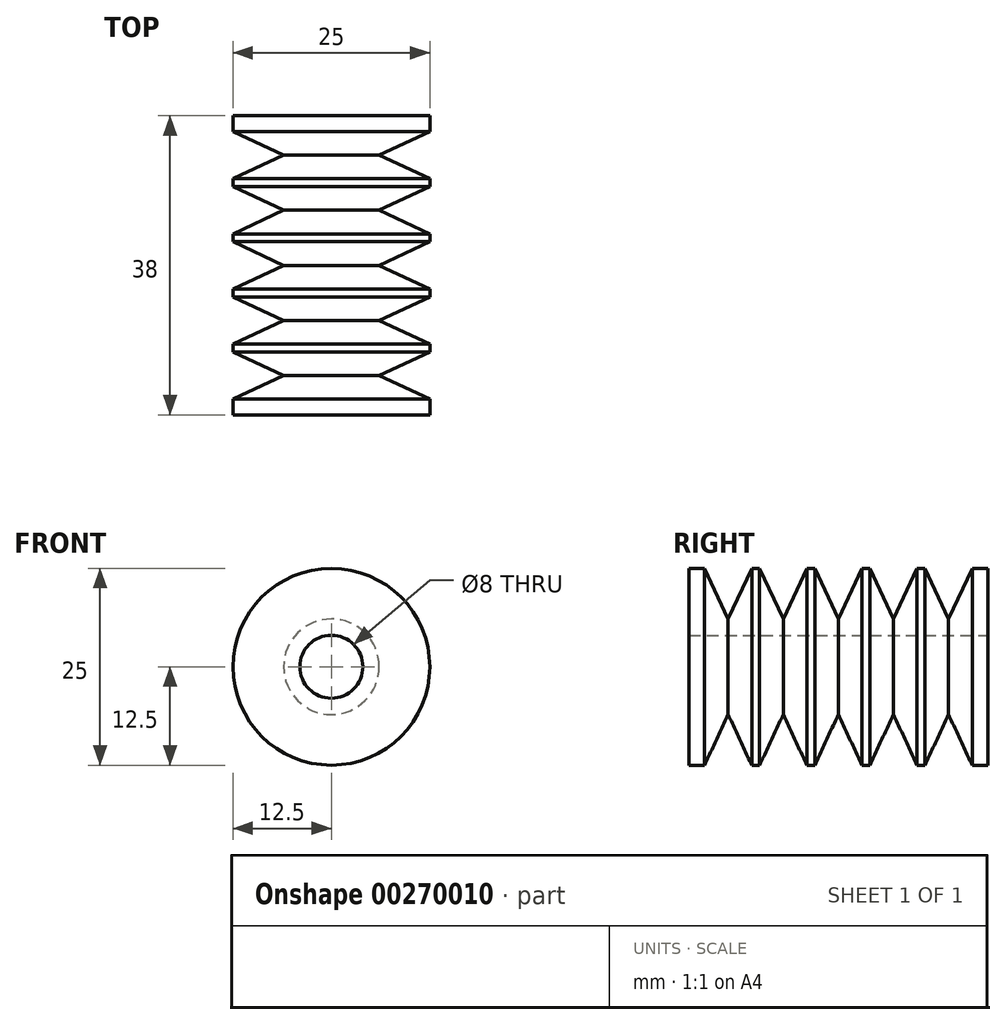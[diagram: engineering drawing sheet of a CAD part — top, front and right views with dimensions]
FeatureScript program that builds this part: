
annotation { "Feature Type Name" : "Feature", "Feature Type Description" : "" }
export const myFeature = defineFeature(function(context is Context, id is Id, definition is map)
    precondition{}
    {
        {
            var Q0;
            Q0=qCreatedBy(makeId("Front.planeOp"),FACE);
            var sketch = newSketch(context, id + "F0", { "sketchPlane" : qUnion([Q0])});
            skCircle(sketch, "E0", {"center": v(0, 0) * mm, "radius": 12.5 * mm});
            skSolve(sketch);
        }
        {
            var Q0;
            Q0 = qSketchRegion(id + "F0", true);
            extrude(context, id + "F1", {"entities" : qUnion([Q0]), "depth" : 5 * mm});
        }
        {
            var Q0;
            Q0=makeQuery(id+"F1.opExtrude","CAP_EDGE",EDGE,{"disambiguationData":[OSD([sQuery(id+"F0.wireOp",EDGE,"E0")])],"isStart":false});
            chamfer(context, id + "F2", {"entities" : qUnion([Q0]), "chamferType" : ChamferType.OFFSET_ANGLE, "width" : 3 * mm, "oppositeDirection" : true, "angle" : 65 * degree, "tangentPropagation" : true});
        }
        {
            var Q0;
            Q0=makeQuery(id+"F1.opExtrude","CAP_FACE",FACE,{"disambiguationData":[OSD([sQuery(id+"F0.wireOp",EDGE,"E0")])],"isStart":false});
            var sketch = newSketch(context, id + "F3", { "sketchPlane" : qUnion([Q0])});
            skCircle(sketch, "E1", {"center": v(0, 0) * mm, "radius": 12.5 * mm});
            skSolve(sketch);
        }
        {
            var Q0;
            Q0 = qSketchRegion(id + "F3", true);
            extrude(context, id + "F4", {"entities" : qUnion([Q0]), "operationType" : NewBodyOperationType.ADD, "depth" : 7 * mm});
        }
        {
            var Q0;
            Q0=makeQuery(id+"F4.opExtrude","CAP_EDGE",EDGE,{"disambiguationData":[OSD([sQuery(id+"F3.wireOp",EDGE,"E1")])],"isStart":true});
            var Q1;
            Q1=makeQuery(id+"F4.opExtrude","CAP_EDGE",EDGE,{"disambiguationData":[OSD([sQuery(id+"F3.wireOp",EDGE,"E1")])],"isStart":false});
            chamfer(context, id + "F5", {"entities" : qUnion([Q0, Q1]), "chamferType" : ChamferType.OFFSET_ANGLE, "width" : 3 * mm, "oppositeDirection" : false, "angle" : 65 * degree, "tangentPropagation" : true});
        }
        {
            var Q0;
            Q0=makeQuery(id+"F4.opExtrude","CAP_FACE",FACE,{"disambiguationData":[OSD([sQuery(id+"F3.wireOp",EDGE,"E1")])],"isStart":false});
            var sketch = newSketch(context, id + "F6", { "sketchPlane" : qUnion([Q0])});
            skCircle(sketch, "E2", {"center": v(0, 0) * mm, "radius": 12.5 * mm});
            skSolve(sketch);
        }
        {
            var Q0;
            Q0 = qSketchRegion(id + "F6", true);
            extrude(context, id + "F7", {"entities" : qUnion([Q0]), "operationType" : NewBodyOperationType.ADD, "depth" : 7 * mm});
        }
        {
            var Q0;
            Q0=makeQuery(id+"F7.opExtrude","CAP_EDGE",EDGE,{"disambiguationData":[OSD([sQuery(id+"F6.wireOp",EDGE,"E2")])],"isStart":true});
            var Q1;
            Q1=makeQuery(id+"F7.opExtrude","CAP_EDGE",EDGE,{"disambiguationData":[OSD([sQuery(id+"F6.wireOp",EDGE,"E2")])],"isStart":false});
            chamfer(context, id + "F8", {"entities" : qUnion([Q0, Q1]), "chamferType" : ChamferType.OFFSET_ANGLE, "width" : 3 * mm, "oppositeDirection" : false, "angle" : 65 * degree, "tangentPropagation" : true});
        }
        {
            var Q0;
            Q0=makeQuery(id+"F7.opExtrude","CAP_FACE",FACE,{"disambiguationData":[OSD([sQuery(id+"F6.wireOp",EDGE,"E2")])],"isStart":false});
            var sketch = newSketch(context, id + "F9", { "sketchPlane" : qUnion([Q0])});
            skCircle(sketch, "E3", {"center": v(0, 0) * mm, "radius": 12.5 * mm});
            skSolve(sketch);
        }
        {
            var Q0;
            Q0 = qSketchRegion(id + "F9", true);
            extrude(context, id + "F10", {"entities" : qUnion([Q0]), "operationType" : NewBodyOperationType.ADD, "depth" : 7 * mm});
        }
        {
            var Q0;
            Q0=makeQuery(id+"F10.opExtrude","CAP_EDGE",EDGE,{"disambiguationData":[OSD([sQuery(id+"F9.wireOp",EDGE,"E3")])],"isStart":true});
            var Q1;
            Q1=makeQuery(id+"F10.opExtrude","CAP_EDGE",EDGE,{"disambiguationData":[OSD([sQuery(id+"F9.wireOp",EDGE,"E3")])],"isStart":false});
            chamfer(context, id + "F11", {"entities" : qUnion([Q0, Q1]), "chamferType" : ChamferType.OFFSET_ANGLE, "width" : 3 * mm, "oppositeDirection" : false, "angle" : 65 * degree, "tangentPropagation" : true});
        }
        {
            var Q0;
            Q0=makeQuery(id+"F10.opExtrude","CAP_FACE",FACE,{"disambiguationData":[OSD([sQuery(id+"F9.wireOp",EDGE,"E3")])],"isStart":false});
            var sketch = newSketch(context, id + "F12", { "sketchPlane" : qUnion([Q0])});
            skCircle(sketch, "E4", {"center": v(0, 0) * mm, "radius": 12.5 * mm});
            skSolve(sketch);
        }
        {
            var Q0;
            Q0 = qSketchRegion(id + "F12", true);
            extrude(context, id + "F13", {"entities" : qUnion([Q0]), "operationType" : NewBodyOperationType.ADD, "depth" : 7 * mm});
        }
        {
            var Q0;
            Q0=makeQuery(id+"F13.opExtrude","CAP_EDGE",EDGE,{"disambiguationData":[OSD([sQuery(id+"F12.wireOp",EDGE,"E4")])],"isStart":true});
            var Q1;
            Q1=makeQuery(id+"F13.opExtrude","CAP_EDGE",EDGE,{"disambiguationData":[OSD([sQuery(id+"F12.wireOp",EDGE,"E4")])],"isStart":false});
            chamfer(context, id + "F14", {"entities" : qUnion([Q0, Q1]), "chamferType" : ChamferType.OFFSET_ANGLE, "width" : 3 * mm, "oppositeDirection" : false, "angle" : 65 * degree, "tangentPropagation" : true});
        }
        {
            var Q0;
            Q0=makeQuery(id+"F13.opExtrude","CAP_FACE",FACE,{"disambiguationData":[OSD([sQuery(id+"F12.wireOp",EDGE,"E4")])],"isStart":false});
            var sketch = newSketch(context, id + "F15", { "sketchPlane" : qUnion([Q0])});
            skCircle(sketch, "E5", {"center": v(0, 0) * mm, "radius": 12.5 * mm});
            skSolve(sketch);
        }
        {
            var Q0;
            Q0 = qSketchRegion(id + "F15", true);
            extrude(context, id + "F16", {"entities" : qUnion([Q0]), "operationType" : NewBodyOperationType.ADD, "depth" : 5 * mm});
        }
        {
            var Q0;
            Q0=makeQuery(id+"F16.opExtrude","CAP_EDGE",EDGE,{"disambiguationData":[OSD([sQuery(id+"F15.wireOp",EDGE,"E5")])],"isStart":true});
            chamfer(context, id + "F17", {"entities" : qUnion([Q0]), "chamferType" : ChamferType.OFFSET_ANGLE, "width" : 3 * mm, "oppositeDirection" : false, "angle" : 65 * degree, "tangentPropagation" : true});
        }
        {
            var Q0;
            Q0=makeQuery(id+"F1.opExtrude","CAP_FACE",FACE,{"disambiguationData":[OSD([sQuery(id+"F0.wireOp",EDGE,"E0")])],"isStart":true});
            var sketch = newSketch(context, id + "F18", { "sketchPlane" : qUnion([Q0])});
            skPoint(sketch, "E6", {"position": v(0, 0) * mm});
            skSolve(sketch);
        }
        {
            var Q0;
            Q0=sQuery(id+"F18.wireOp",VERTEX,"E6");
            var Q1;
            Q1=makeQuery(id+"F1.opExtrude","SWEPT_BODY",BODY,{"disambiguationData":[OSD([sQuery(id+"F0.wireOp",EDGE,"E0")])]});
            hole(context, id + "F19", {"style" : HoleStyle.SIMPLE, "endStyle" : HoleEndStyle.THROUGH, "holeDiameter" : 8 * mm, "tappedDepth" : 12 * mm, "tapClearance" : 3, "locations" : qUnion([Q0]), "scope" : qUnion([Q1])});
        }
    });
